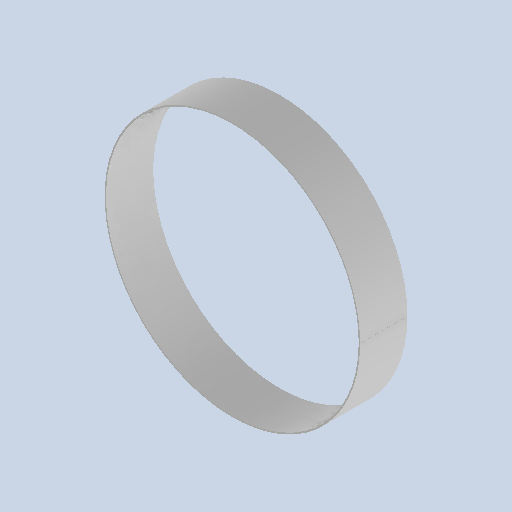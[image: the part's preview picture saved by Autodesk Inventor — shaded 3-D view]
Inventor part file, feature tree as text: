
AUTODESK INVENTOR PART (.ipt)
format: ipt  version: 2025 (Build 290162010, 162A)  size: 173,056 bytes
history: native  units: mm
features: revolve x1, sketch x1, other x1
ambient origin geometry x8: Origin, YZ Plane, XZ Plane, XY Plane, X Axis, Y Axis, Z Axis, Center Point
bodies: Solid1 (feature_tree)
feature tree (3):
  revolve  "Revolution1"  [1 undecoded]
  sketch  "Sketch3"  dims[d1=3.0mm d2=100.0mm d3=270.0mm d4=62.8144mm]
  other  "Definition1"
note: 1 required parameter value undecoded (feature->parameter linkage not recoverable at this tier; creation-order binding heuristic only, values carry confidence <= 0.55)
